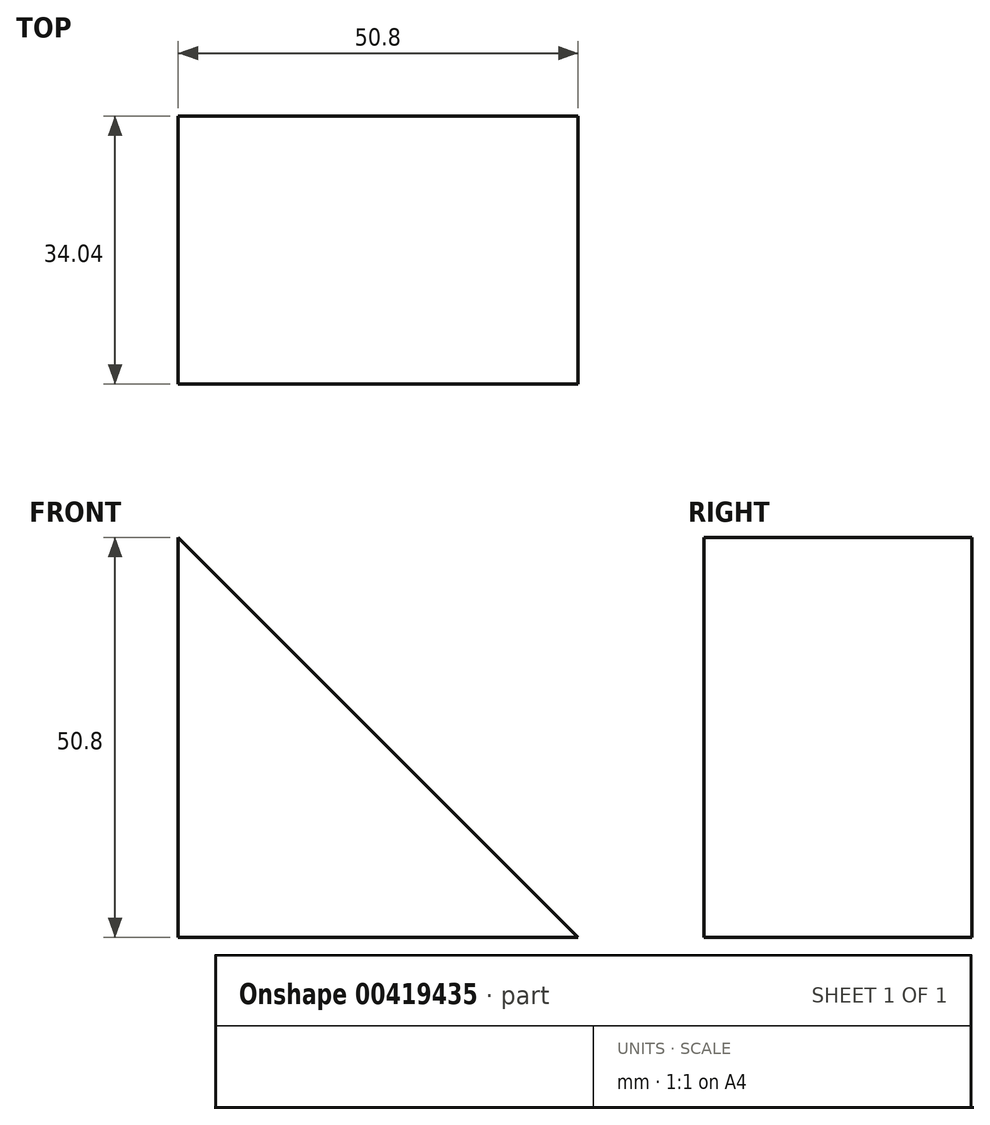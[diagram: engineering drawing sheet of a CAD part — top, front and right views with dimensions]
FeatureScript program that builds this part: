
annotation { "Feature Type Name" : "Feature", "Feature Type Description" : "" }
export const myFeature = defineFeature(function(context is Context, id is Id, definition is map)
    precondition{}
    {
        {
            var Q0;
            Q0=qCreatedBy(makeId("Front.planeOp"),FACE);
            var sketch = newSketch(context, id + "F0", { "sketchPlane" : qUnion([Q0])});
            skLineSegment(sketch, "E0.top", {"start": v(25.4, -25.4) * mm, "end": v(-25.4, -25.4) * mm});
            skLineSegment(sketch, "E0.right", {"start": v(-25.4, 25.4) * mm, "end": v(-25.4, -25.4) * mm});
            skPoint(sketch, "E0.middle", {"position": v(0, 0) * mm});
            skLineSegment(sketch, "E1", {"start": v(-25.4, 25.4) * mm, "end": v(25.4, -25.4) * mm});
            skPoint(sketch, "E0.left.start.orphan", {"position": v(25.4, 25.4) * mm});
            skSolve(sketch);
        }
        {
            var Q0;
            Q0 = qSketchRegion(id + "F0", true);
            extrude(context, id + "F1", {"entities" : qUnion([Q0]), "depth" : 34.04 * mm});
        }
    });
